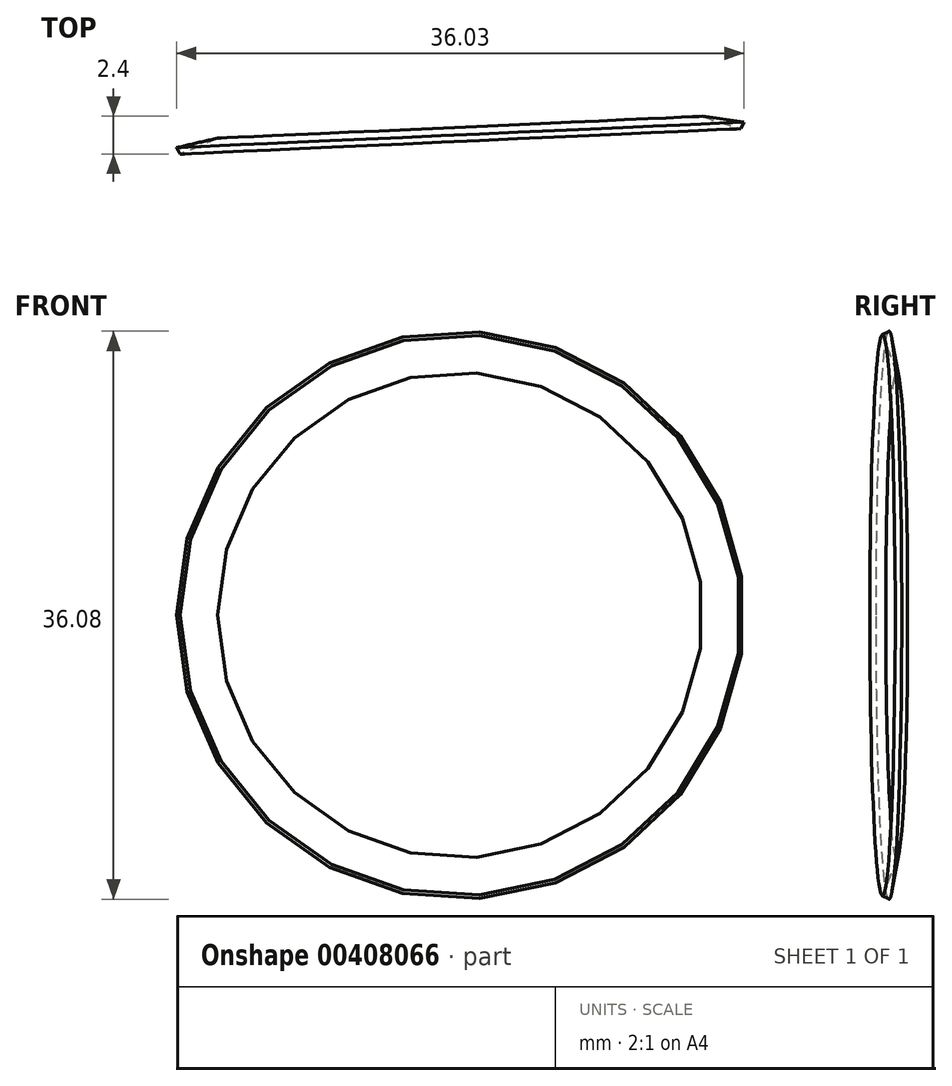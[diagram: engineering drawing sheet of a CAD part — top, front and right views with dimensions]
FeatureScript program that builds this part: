
annotation { "Feature Type Name" : "Feature", "Feature Type Description" : "" }
export const myFeature = defineFeature(function(context is Context, id is Id, definition is map)
    precondition{}
    {
        {
            var Q0;
            Q0=qCreatedBy(makeId("Top.planeOp"),FACE);
            var sketch = newSketch(context, id + "F0", { "sketchPlane" : qUnion([Q0])});
            skArc(sketch, "E0", {"start": v(4.86, 38.62) * mm, "mid": v(5.7, 72.36) * mm, "end": v(-14.22, 45.11) * mm});
            skFitSpline(sketch, "E1", {"points": [v(-30.44, 17.33) * mm, v(-31.7, 7.77) * mm, v(-25, 0) * mm, v(-31.7, -5.03) * mm, v(-26.21, -12.65) * mm, v(-31.09, -19.66) * mm, v(-25.9, -28.5) * mm], "startDerivative": vector(-27.56, -58.64) * mm, "endDerivative": vector(53.28, -53.1) * mm});
            skFitSpline(sketch, "E2", {"points": [v(-21.67, 15.4) * mm, v(-23.77, 8.08) * mm, v(-17.68, 0) * mm, v(-21.34, -6.86) * mm, v(-14.02, -15.09) * mm, v(-19.81, -22.1) * mm, v(-14.94, -29.41) * mm], "startDerivative": vector(-31.7, -48.96) * mm, "endDerivative": vector(53.45, -45.43) * mm});
            skFitSpline(sketch, "E3", {"points": [v(20.73, 9.03) * mm, v(11.28, -4.72) * mm, v(20.12, -12.34) * mm, v(14.63, -23.93) * mm, v(40.23, -28.5) * mm, v(33.83, -10.21) * mm, v(55.47, -2.6) * mm, v(42.48, 9.23) * mm], "startDerivative": vector(-123.7, -111.74) * mm, "endDerivative": vector(-165.44, 100.11) * mm});
            skFitSpline(sketch, "E4", {"points": [v(-25.9, -28.5) * mm, v(-36.58, -36.12) * mm, v(-25.9, -50.75) * mm, v(0, -41.91) * mm, v(-14.94, -29.41) * mm], "startDerivative": vector(-70.2, -26.1) * mm, "endDerivative": vector(-96.84, 47.58) * mm});
            skFitSpline(sketch, "E5", {"points": [v(-8.26, 15.31) * mm, v(-6.1, -6.55) * mm, v(0, -15.4) * mm, v(8.53, -45.57) * mm, v(19.5, -56.85) * mm], "startDerivative": vector(-0.19, -96.14) * mm, "endDerivative": vector(54.31, -35.53) * mm});
            skFitSpline(sketch, "E6", {"points": [v(-3.35, 15.4) * mm, v(0, 0) * mm, v(7.01, -6.86) * mm, v(7.32, -21.18) * mm, v(14.63, -41.91) * mm, v(32.3, -48.31) * mm, v(61.26, -48.31) * mm], "startDerivative": vector(6.67, -112.98) * mm, "endDerivative": vector(142.17, 5.24) * mm});
            skFitSpline(sketch, "E7", {"points": [v(19.5, -56.85) * mm, v(61.26, -60.5) * mm, v(64.62, -67.82) * mm, v(51.82, -70.56) * mm, v(77.72, -79.1) * mm, v(71.93, -56.85) * mm, v(86.87, -53.19) * mm, v(80.77, -35.5) * mm, v(61.26, -48.31) * mm], "startDerivative": vector(279.1, 13.4) * mm, "endDerivative": vector(-152.36, -176.7) * mm});
            skFitSpline(sketch, "E8", {"points": [v(68.07, -40.41) * mm, v(68.07, -6.86) * mm, v(74.98, -2.6) * mm, v(80.77, -3.2) * mm, v(55.17, 21.18) * mm, v(64.62, 25.45) * mm, v(49.99, 42.21) * mm, v(62.79, 42.21) * mm, v(39.32, 55.63) * mm, v(34.75, 45.57) * mm, v(27.74, 50.75) * mm, v(28.65, 59.9) * mm, v(45.72, 62.94) * mm, v(60.35, 66.9) * mm, v(68.07, 64.16) * mm, v(75.6, 47.1) * mm, v(86.87, 39.47) * mm, v(75.29, 23.62) * mm, v(92.66, 20.57) * mm, v(91.44, 4.72) * mm, v(80.77, 9.9) * mm, v(89.61, -10.21) * mm, v(85.65, -14.78) * mm, v(92.35, -20.88) * mm, v(85.65, -24.23) * mm, v(94.18, -25.76) * mm, v(84.12, -38.44) * mm], "startDerivative": vector(-68.05, 688.9) * mm, "endDerivative": vector(-462.82, -390.56) * mm});
            skFitSpline(sketch, "E9.trimOffspring", {"points": [v(-14.22, 45.11) * mm, v(-29.57, 32.46) * mm, v(-35.05, 39.78) * mm, v(-35.36, 42.52) * mm, v(-46.33, 39.17) * mm, v(-34.14, 19.05) * mm, v(-3.35, 15.4) * mm, v(5.8, 16.61) * mm, v(-3.05, 27.89) * mm, v(11.28, 24.84) * mm, v(25.3, 5.03) * mm, v(45.72, 13.56) * mm, v(4.86, 38.62) * mm], "startDerivative": vector(-185.87, -228.8) * mm, "endDerivative": vector(-467.47, 183.25) * mm});
            skFitSpline(sketch, "E10", {"points": [v(-19.73, 38.33) * mm, v(-29.57, 32.46) * mm, v(-34.96, 38.33) * mm, v(-35.36, 42.52) * mm, v(-46.33, 39.17) * mm, v(-34.14, 19.05) * mm, v(-30.44, 17.33) * mm], "startDerivative": vector(-54.95, -52.16) * mm, "endDerivative": vector(25.18, -3.51) * mm});
            skFitSpline(sketch, "E11", {"points": [v(-14.22, 45.11) * mm, v(-19.73, 38.33) * mm], "startDerivative": vector(-5.5, -6.78) * mm, "endDerivative": vector(-5.5, -6.78) * mm});
            skFitSpline(sketch, "E12.trimOffspring", {"points": [v(-14.22, 45.11) * mm, v(-29.57, 32.46) * mm, v(-35.05, 39.78) * mm, v(-35.36, 42.52) * mm, v(-46.33, 39.17) * mm, v(-34.14, 19.05) * mm, v(-3.35, 15.4) * mm, v(5.8, 16.61) * mm, v(-3.05, 27.89) * mm, v(11.28, 24.84) * mm, v(25.3, 5.03) * mm, v(45.72, 13.56) * mm, v(4.86, 38.62) * mm], "startDerivative": vector(-185.87, -228.8) * mm, "endDerivative": vector(-467.47, 183.25) * mm});
            skLineSegment(sketch, "E13", {"start": v(68.07, -40.41) * mm, "end": v(61.26, -48.31) * mm});
            skLineSegment(sketch, "E14", {"start": v(-48.57, 76.91) * mm, "end": v(-40.65, -98.38) * mm});
            skSolve(sketch);
        }
        {
            var Q0;
            Q0=makeQuery(id+"F0.imprint","IMPRINT",FACE,{"disambiguationData":[TD([[makeQuery(id+"F0.imprint","IMPRINT",EDGE,{"derivedFrom":sQuery(id+"F0.wireOp",EDGE,"E0")}),1.0]])]});
            var Q1;
            Q1=sQuery(id+"F0.wireOp",EDGE,"E14");
            revolve(context, id + "F1", {"entities" : qUnion([Q0]), "axis" : qUnion([Q1]), "revolveType" : RevolveType.FULL});
        }
        {
            var Q0;
            Q0=makeQuery(id+"F1.opRevolve","SWEPT_FACE",FACE,{"disambiguationData":[OSD([sQuery(id+"F0.wireOp",EDGE,"E10")])]});
            var Q1;
            Q1=makeQuery(id+"F1.opRevolve","SWEPT_FACE",FACE,{"disambiguationData":[OSD([sQuery(id+"F0.wireOp",EDGE,"E0")])]});
            var Q2;
            Q2=makeQuery(id+"F1.opRevolve","SWEPT_FACE",FACE,{"disambiguationData":[OSD([sQuery(id+"F0.wireOp",EDGE,"E11")])]});
            var Q3;
            Q3=makeQuery(id+"F1.opRevolve","SWEPT_FACE",FACE,{"disambiguationData":[OSD([sQuery(id+"F0.wireOp",EDGE,"E8")])]});
            var Q4;
            Q4=makeQuery(id+"F1.opRevolve","SWEPT_FACE",FACE,{"disambiguationData":[OSD([sQuery(id+"F0.wireOp",EDGE,"E7")])]});
            var Q5;
            Q5=makeQuery(id+"F1.opRevolve","SWEPT_FACE",FACE,{"disambiguationData":[OSD([sQuery(id+"F0.wireOp",EDGE,"E9.trimOffspring")])]});
            shell(context, id + "F2", {"entities" : qUnion([Q0, Q1, Q2, Q3, Q4, Q5]), "thickness" : 2.54 * mm});
        }
    });
